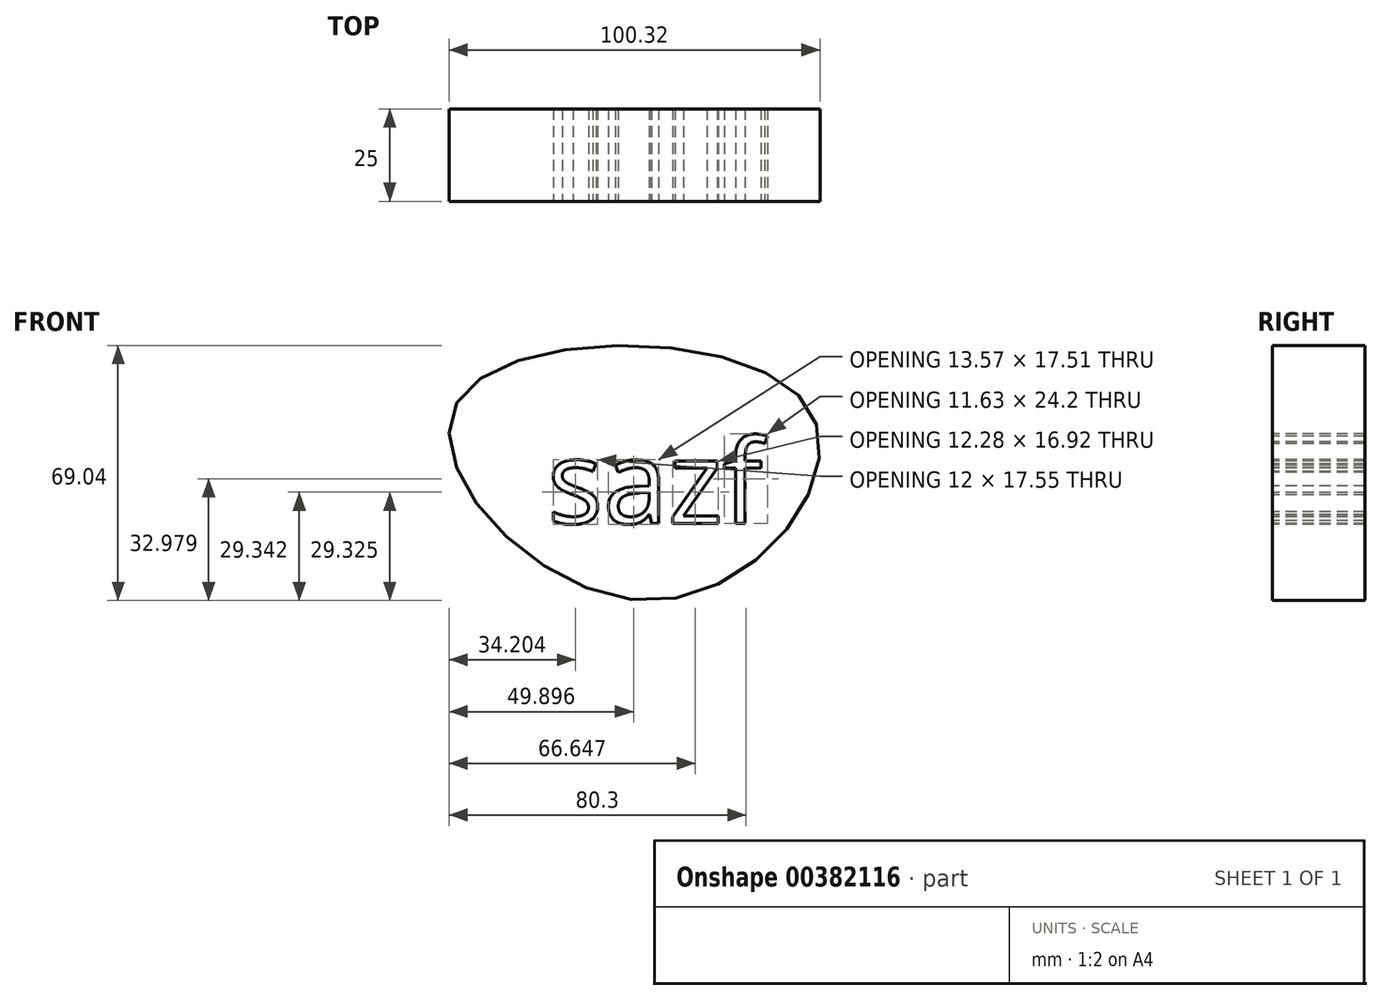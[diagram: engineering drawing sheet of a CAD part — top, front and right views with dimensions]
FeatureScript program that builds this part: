
annotation { "Feature Type Name" : "Feature", "Feature Type Description" : "" }
export const myFeature = defineFeature(function(context is Context, id is Id, definition is map)
    precondition{}
    {
        {
            var Q0;
            Q0=qCreatedBy(makeId("Front.planeOp"),FACE);
            var sketch = newSketch(context, id + "F0", { "sketchPlane" : qUnion([Q0])});
            skFitSpline(sketch, "E0", {"points": [v(-53.53, 33.93) * mm, v(0, -19.6) * mm, v(41.55, 32.84) * mm, v(-53.53, 33.93) * mm]});
            skSolve(sketch);
        }
        {
            var Q0;
            Q0 = qSketchRegion(id + "F0", true);
            extrude(context, id + "F1", {"entities" : qUnion([Q0]), "depth" : 25 * mm});
        }
        {
            var Q0;
            Q0=makeQuery(id+"F1.opExtrude","CAP_FACE",FACE,{"disambiguationData":[OSD([sQuery(id+"F0.wireOp",EDGE,"E0")])],"isStart":false});
            var sketch = newSketch(context, id + "F2", { "sketchPlane" : qUnion([Q0])});
            skText(sketch, "E1", { "text": "sazf", "fontName": "OpenSans-Regular.ttf"});
            const initialGuessF2  = {"E1": [-0.029, 0.00126, 1, 0, 0.02277]};
            skSetInitialGuess(sketch, initialGuessF2);
            skSolve(sketch);
        }
        {
            var Q0;
            Q0 = qSketchRegion(id + "F2", true);
            extrude(context, id + "F3", {"entities" : qUnion([Q0]), "operationType" : NewBodyOperationType.REMOVE, "endBound" : BoundingType.THROUGH_ALL, "oppositeDirection" : true, "depth" : 25 * mm});
        }
    });
